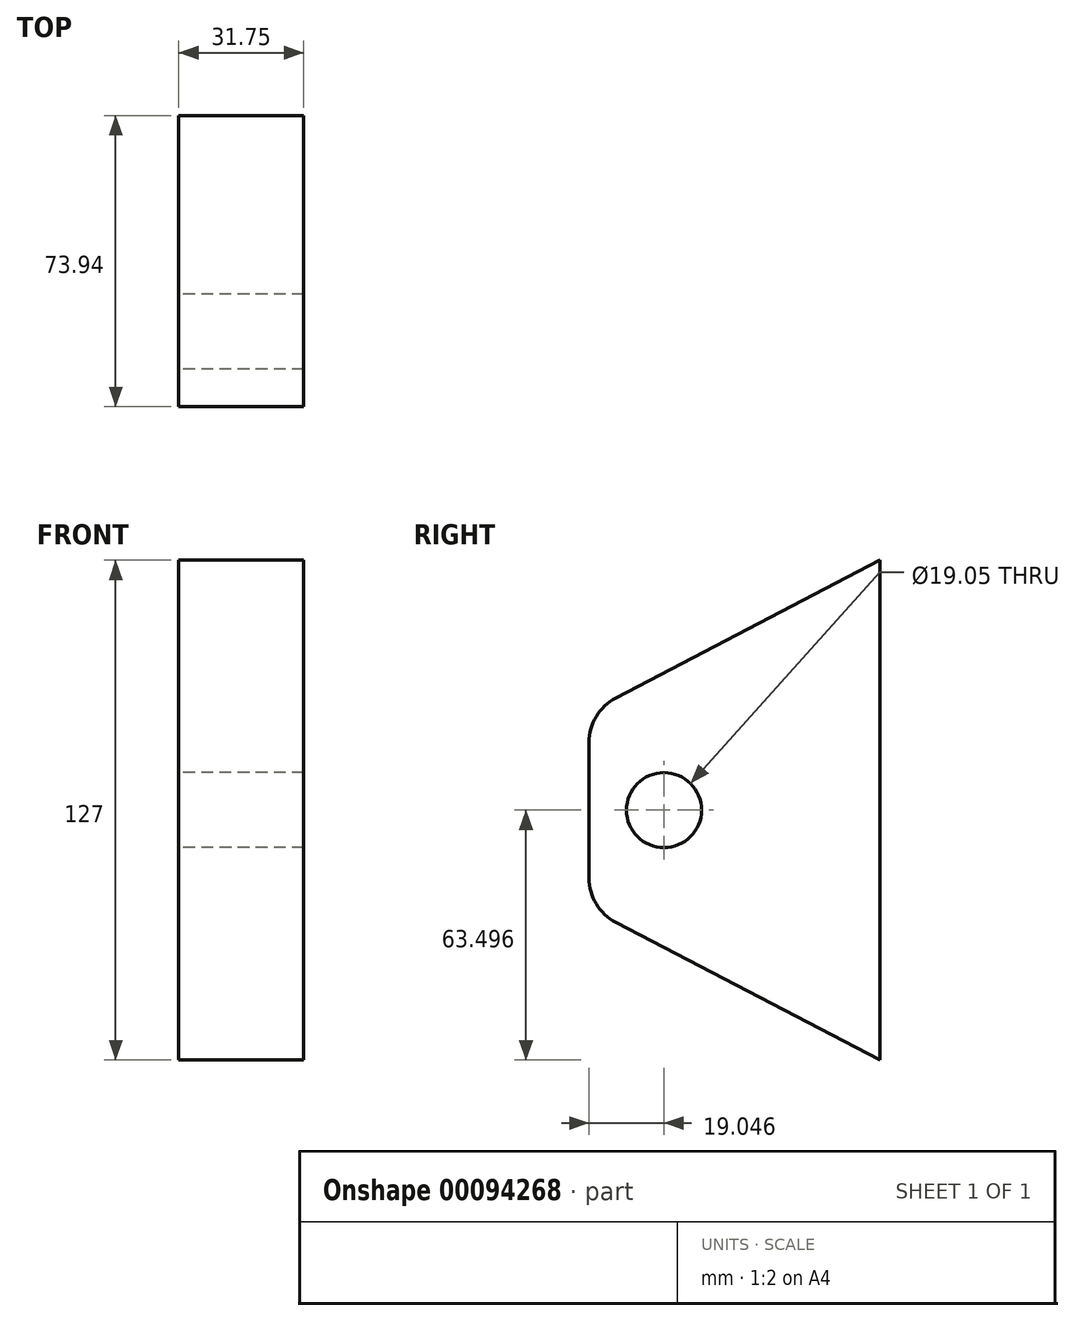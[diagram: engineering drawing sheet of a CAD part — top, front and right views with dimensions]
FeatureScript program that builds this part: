
annotation { "Feature Type Name" : "Feature", "Feature Type Description" : "" }
export const myFeature = defineFeature(function(context is Context, id is Id, definition is map)
    precondition{}
    {
        {
            var Q0;
            Q0=qCreatedBy(makeId("Right.planeOp"),FACE);
            var sketch = newSketch(context, id + "F0", { "sketchPlane" : qUnion([Q0])});
            skLineSegment(sketch, "E0.left", {"start": v(36.97, 72.7) * mm, "end": v(36.97, -54.3) * mm});
            skLineSegment(sketch, "E0.right", {"start": v(-36.97, 26.46) * mm, "end": v(-36.97, -8.06) * mm});
            skPoint(sketch, "E0.middle", {"position": v(0, 0) * mm});
            skPoint(sketch, "E1.visualSharp", {"position": v(-36.97, 54.3) * mm});
            skPoint(sketch, "E2.visualSharp", {"position": v(-36.97, -72.7) * mm});
            skLineSegment(sketch, "E3", {"start": v(-30.14, 37.72) * mm, "end": v(36.97, 72.7) * mm});
            skLineSegment(sketch, "E4", {"start": v(-30.14, -19.33) * mm, "end": v(36.97, -54.3) * mm});
            skPoint(sketch, "E5.visualSharp", {"position": v(-36.97, 34.16) * mm});
            skArc(sketch, "E5.filletArc", {"start": v(-30.14, 37.72) * mm, "mid": v(-35.13, 33.04) * mm, "end": v(-36.97, 26.46) * mm});
            skPoint(sketch, "E6.visualSharp", {"position": v(-36.97, -15.77) * mm});
            skArc(sketch, "E6.filletArc", {"start": v(-36.97, -8.06) * mm, "mid": v(-35.13, -14.65) * mm, "end": v(-30.14, -19.33) * mm});
            skLineSegment(sketch, "E7", {"start": v(-36.97, 9.2) * mm, "end": v(36.97, 9.2) * mm});
            skCircle(sketch, "E8", {"center": v(-17.92, 9.2) * mm, "radius": 9.53 * mm});
            skSolve(sketch);
        }
        {
            var Q0;
            Q0 = qSketchRegion(id + "F0", true);
            extrude(context, id + "F1", {"entities" : qUnion([Q0]), "depth" : 31.75 * mm});
        }
    });
